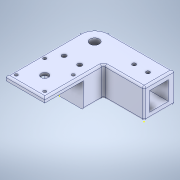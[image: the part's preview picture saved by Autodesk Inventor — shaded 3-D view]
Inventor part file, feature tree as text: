
AUTODESK INVENTOR PART (.ipt)
format: ipt  version: 2020 (Build 240168000, 168)  size: 181,760 bytes
history: imported  units: in
note: dims shown in document units (in); Inventor stores cm internally (conversion verified against a paired STEP export)
features: sketch x6, other x1, imported_body x1
ambient origin geometry x8: Origin, YZ Plane, XZ Plane, XY Plane, X Axis, Y Axis, Z Axis, Center Point
bodies: Solid1 (imported_parasolid)
feature tree (8):
  sketch  "Sketch1"
  sketch  "Sketch3"
  sketch  "Sketch4"
  sketch  "Sketch5"
  sketch  "Sketch6"
  sketch  "Sketch7"
  other  "Cut-Extrude11"
  imported_body  NMx_Import_Brep_tag  [imported B-rep: ~49 faces, bbox_mm=[86.2, 32.4, 96.21]]
